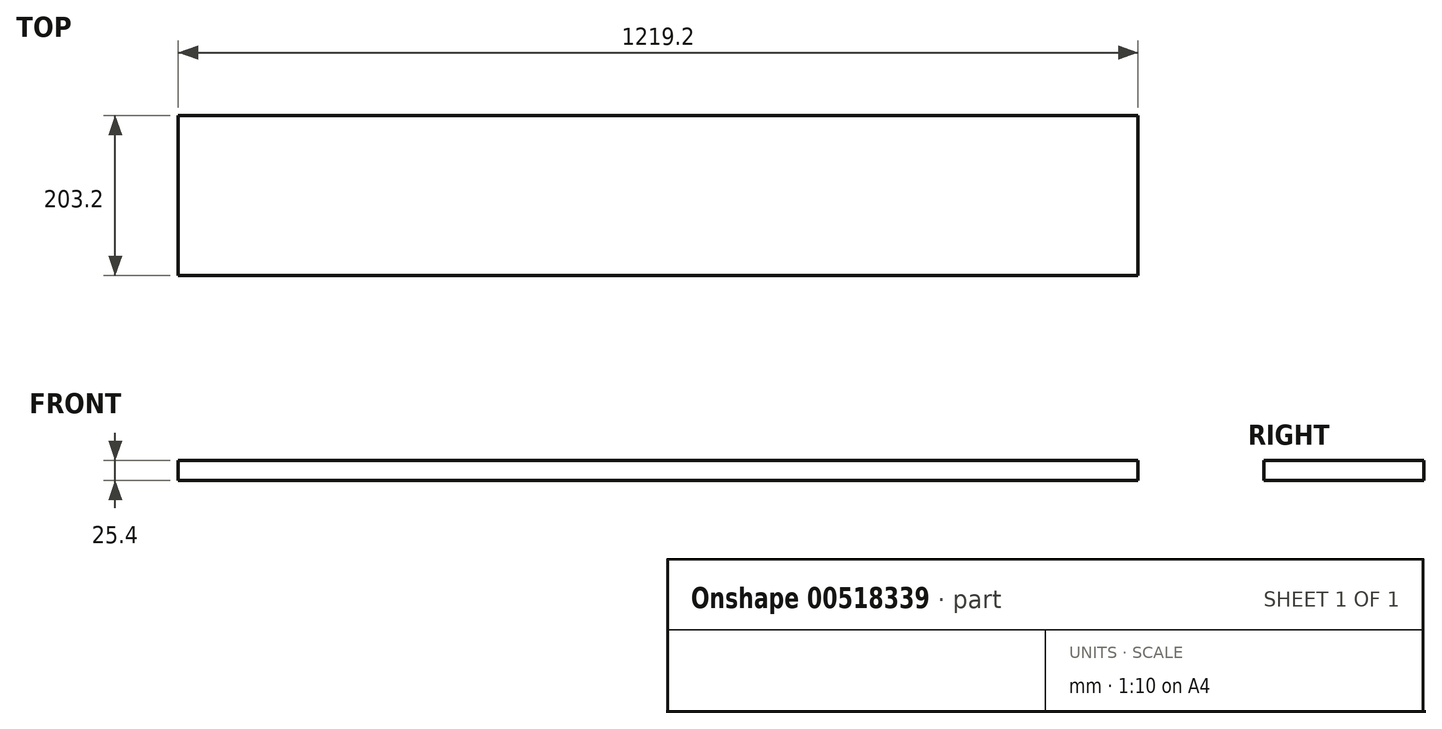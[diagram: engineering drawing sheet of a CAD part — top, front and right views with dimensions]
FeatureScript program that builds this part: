
annotation { "Feature Type Name" : "Feature", "Feature Type Description" : "" }
export const myFeature = defineFeature(function(context is Context, id is Id, definition is map)
    precondition{}
    {
        {
            var Q0;
            Q0=qCreatedBy(makeId("Top.planeOp"),FACE);
            var sketch = newSketch(context, id + "F0", { "sketchPlane" : qUnion([Q0])});
            skLineSegment(sketch, "E0.bottom", {"start": v(-609.6, 101.6) * mm, "end": v(609.6, 101.6) * mm});
            skLineSegment(sketch, "E0.top", {"start": v(-609.6, -101.6) * mm, "end": v(609.6, -101.6) * mm});
            skLineSegment(sketch, "E0.left", {"start": v(-609.6, 101.6) * mm, "end": v(-609.6, -101.6) * mm});
            skLineSegment(sketch, "E0.right", {"start": v(609.6, 101.6) * mm, "end": v(609.6, -101.6) * mm});
            skPoint(sketch, "E0.middle", {"position": v(0, 0) * mm});
            skSolve(sketch);
        }
        {
            var Q0;
            Q0=makeQuery(id+"F0.imprint","IMPRINT",FACE,{"disambiguationData":[TD([[makeQuery(id+"F0.imprint","IMPRINT",EDGE,{"derivedFrom":sQuery(id+"F0.wireOp",EDGE,"E0.bottom")}),-1.0]])]});
            extrude(context, id + "F1", {"entities" : qUnion([Q0]), "depth" : 25.4 * mm, "offsetDistance" : 25.4 * mm});
        }
    });
